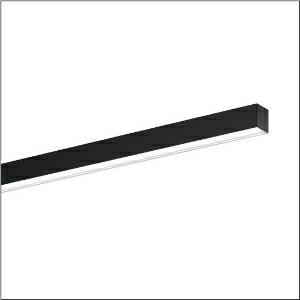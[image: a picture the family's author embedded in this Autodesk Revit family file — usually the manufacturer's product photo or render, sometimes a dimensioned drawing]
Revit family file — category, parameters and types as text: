
# Revit family: silica_r__21_51mx20da32bb_5abe
name_source: partatom
category: Lighting Fixtures
units: mm (PartAtom-declared; Revit-internal decimal feet)

## family parameters
Cut with Voids When Loaded = No
Host = Face
Light Source = No
Part Type = Normal
Room Calculation Point = No
Round Connector Dimension = Use Diameter
Shared = No

## types (1)
- --- (1 x LED, 2400 lm, 16.1 W, 3000K)
    Apparent Load = 16 VA
    CIE Flux Codes = 48 79 96 100 100
    Color Rendering = 80
    Color Temperature = 3000K
    Default Elevation = 1800 mm
    Description = Silica® 21, office luminaire, primary optical cover: cover, of PMMA, opal, light emission: direct distribution, primary light characteristic: symmetric, installation type: surface-mounted, LED, rated luminous flux: 2.400lm, luminous efficacy: 149lm/W, light colour: 830, colour temperature: 3000K, control gear: DALI 2, with terminal, 3+2-pole, max. 2.5mm², mains connection: 220..240V, AC, 50/60Hz, rated input power: 16.1W, luminaire housing, of aluminium, matt jet black (RAL 9005), length: 1.204mm, width: 53mm, height: 53mm, protection rating (complete): IP20, insulation class (complete): insulation class I (protective earthing), certification: CE, permissible operating ambient temperature: 0..+35°C, standard: EN 50419, packaging unit: 1 piece
    Height = 53 mm
    Lamp = 1 x LED
    Lamp Light Flux = 2400 lm
    Lamp Power = 16.1 W
    Lamp count = 1
    Length = 1204 mm
    Luminous efficacy = 149 lm/W
    Manufacturer = Siteco
    ModVariant = No
    Model = 51MX20DA32BB
    Mounting Place = Ceiling
    Mounting Type = Surface mounted
    Number of Poles = 1
    OnlyDefault = Yes
    Power Factor = 1
    Product Name = Silica® 21
    Product group = office luminaire | ceiling mounted
    ProductGroupID = 303
    Protection Class = Protection class I
    Protection Degree = IP 20
    RLX_Detail_Level = 1
    RLX_Emergency_Light_Flux = 0 lm
    RLX_Emergency_Type = 0
    RLX_Emergency_Type_DB = No
    RlxData = <blob elided: 28741 chars, md5=f8ba6fe8>
    Socket = socket
    Standby Power = 0 W
    System Light Flux = 2400 lm
    System Power = 16 W
    Type Comments = factory setting: luminous flux: 100 % | dim-lin: 254 | 233 mA
    Type Image = l_1335925.jpg
    URL = http://relux.com
    VarID = @adj_026707
    Voltage = 0 V
    Weight = 0.00 kg
    Width = 53 mm

## geometry (parser evidence)
native form markers: Blend x4, Sweep x8
no freeform markers — native parametric forms only
